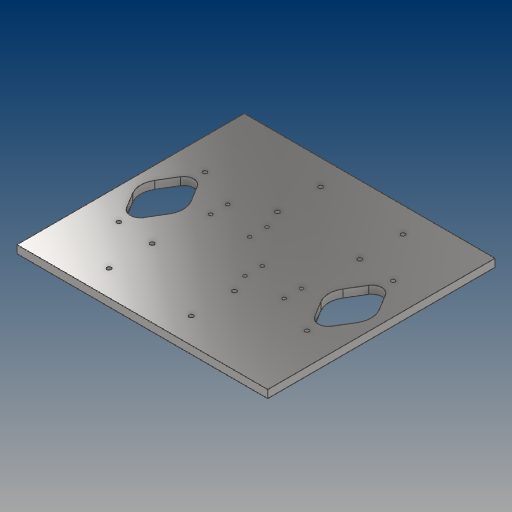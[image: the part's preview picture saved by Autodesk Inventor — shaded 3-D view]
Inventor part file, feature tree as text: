
AUTODESK INVENTOR PART (.ipt)
format: ipt  version: 2021 (Build 250183000, 183)  size: 206,848 bytes
history: native  units: mm
features: reference x17, other x6, sketch x5, hole x3, extrude x2, mirror x1, projected_geometry x1
ambient origin geometry x8: Origin, YZ Plane, XZ Plane, XY Plane, X Axis, Y Axis, Z Axis, Center Point
bodies: Solid1 (feature_tree)
feature tree (35):
  extrude  "Extrusion1"  Depth=320.0mm
  extrude  "Extrusion2"  Depth=54.0mm
  hole  "Hole2"  [1 undecoded]
  mirror  "Mirror1"
  hole  "Hole3"  [1 undecoded]
  hole  "Hole4"  [1 undecoded]
  sketch  "Sketch1"  dims[d0=290.0mm d1=320.0mm]
  sketch  "Sketch3"  dims[d2=10.0mm d3=0.0mm d13=54.0mm]
  sketch  "Sketch4"  dims[d14=25.0mm d15=25.0mm d16=0.0mm]
  projected_geometry  "Projected Loop2"
  sketch  "Sketch5"  dims[d17=55.0mm]
  reference  "Reference1"
  reference  "Reference2"
  reference  "Reference3"
  reference  "Reference4"
  reference  "Reference5"
  reference  "Reference6"
  reference  "Reference7"
  reference  "Reference8"
  reference  "Reference9"
  sketch  "Sketch6"  dims[d18=5.2mm d19=6.0mm d20=4.0mm d21=2.0mm d22=90.0deg d23=8.0mm d24=20.594885mm d25=5.5mm d26=6.0mm d27=4.0mm d28=2.0mm d29=90.0deg d30=8.0mm d31=20.594885mm d32=4.4mm d33=6.0mm d34=4.0mm d35=2.0mm d36=90.0deg d37=8.0mm d38=20.594885mm]
  reference  "Reference10"
  reference  "Reference11"
  reference  "Reference12"
  reference  "Reference13"
  reference  "Reference14"
  reference  "Reference15"
  reference  "Reference16"
  reference  "Reference17"
  other  "0002_Part_De_xe.iam"
  other  "0001_ASS_Hop_so:1"
  other  "22_Hop_so_ngang:2"
  other  "22_Hop_so_ngang:1"
  other  "0001_ASS_Hop_so:2"
  other  "08_Ga_dong_co_02:1"
note: 3 required parameter values undecoded (feature->parameter linkage not recoverable at this tier; creation-order binding heuristic only, values carry confidence <= 0.55)
